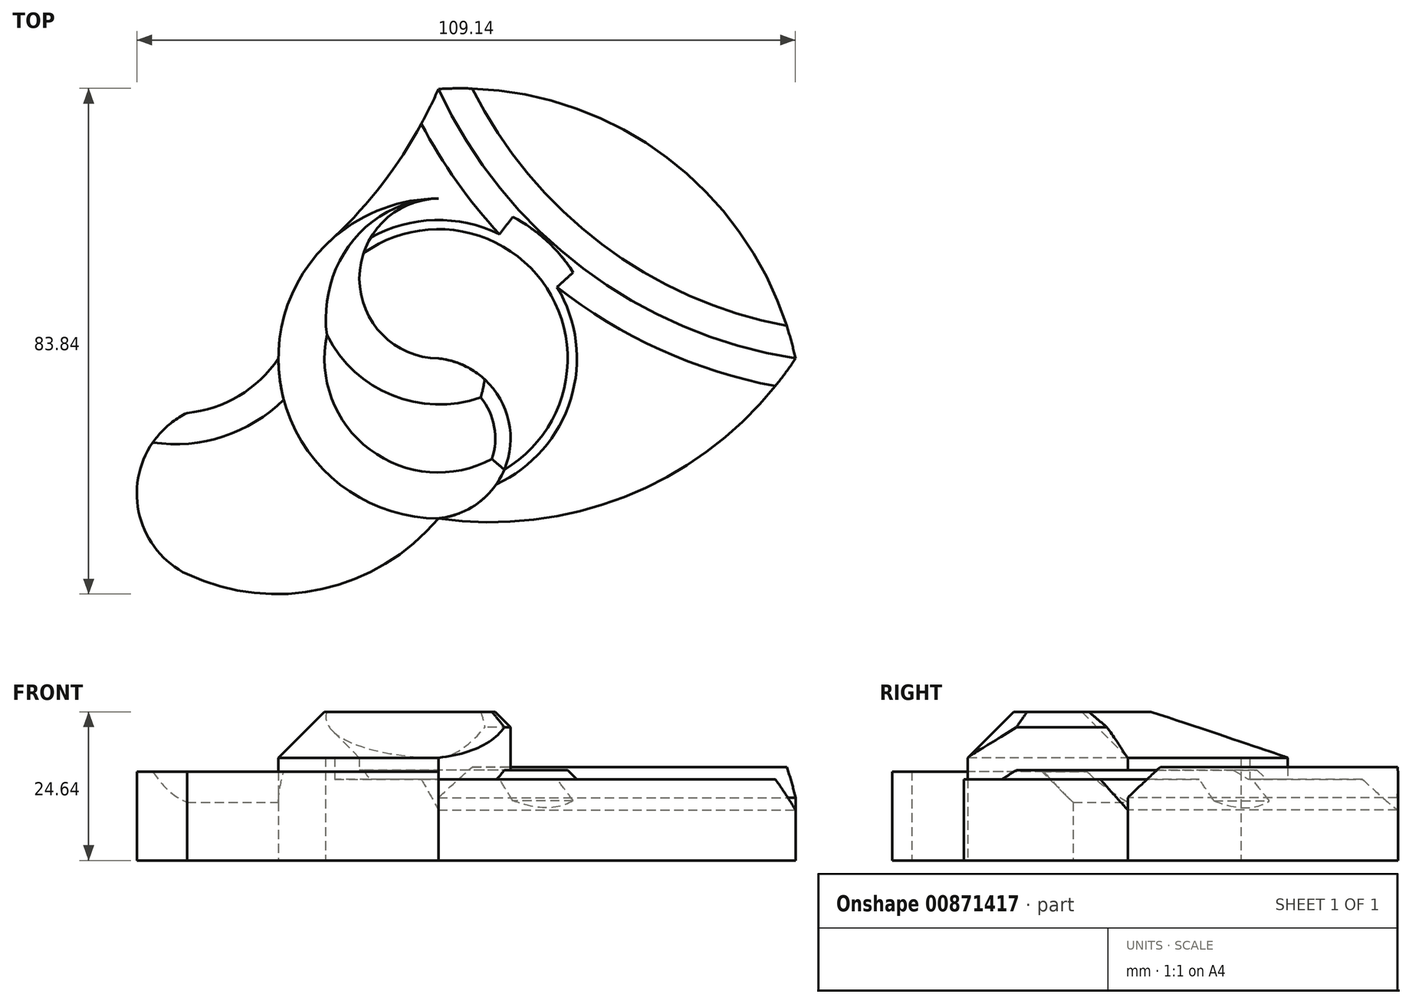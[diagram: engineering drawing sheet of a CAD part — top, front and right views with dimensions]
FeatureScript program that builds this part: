
annotation { "Feature Type Name" : "Feature", "Feature Type Description" : "" }
export const myFeature = defineFeature(function(context is Context, id is Id, definition is map)
    precondition{}
    {
        {
            var Q0;
            Q0=qCreatedBy(makeId("Top.planeOp"),FACE);
            var sketch = newSketch(context, id + "F0", { "sketchPlane" : qUnion([Q0])});
            skCircle(sketch, "E0", {"center": v(0, 0) * mm, "radius": 26.5 * mm});
            skArc(sketch, "E1", {"start": v(0, -26.5) * mm, "mid": v(11.97, -13.25) * mm, "end": v(0, 0) * mm});
            skArc(sketch, "E2", {"start": v(0, 26.5) * mm, "mid": v(-13.1, 13.25) * mm, "end": v(0, 0) * mm});
            skArc(sketch, "E3", {"start": v(-60.7, 0) * mm, "mid": v(-43.6, -9.12) * mm, "end": v(-26.5, 0) * mm});
            skArc(sketch, "E4", {"start": v(0, 44.66) * mm, "mid": v(-40.04, 35.5) * mm, "end": v(-60.7, 0) * mm});
            skArc(sketch, "E5", {"start": v(-60.7, 0) * mm, "mid": v(-24.36, 14.18) * mm, "end": v(0, 44.66) * mm});
            skArc(sketch, "E6", {"start": v(0, -26.5) * mm, "mid": v(33.44, -21.85) * mm, "end": v(59.17, 0) * mm});
            skArc(sketch, "E7", {"start": v(59.17, 0) * mm, "mid": v(37.87, 33.3) * mm, "end": v(0, 44.66) * mm});
            skArc(sketch, "E8", {"start": v(0, 44.66) * mm, "mid": v(24, 14.92) * mm, "end": v(59.17, 0) * mm});
            skArc(sketch, "E9", {"start": v(-41.65, -35.76) * mm, "mid": v(-19.25, -38.22) * mm, "end": v(0, -26.5) * mm});
            skArc(sketch, "E10", {"start": v(-41.65, -9.03) * mm, "mid": v(-49.97, -22.4) * mm, "end": v(-41.65, -35.76) * mm});
            skArc(sketch, "E11", {"start": v(-30.95, -26.5) * mm, "mid": v(-29.13, -13.38) * mm, "end": v(-41.65, -9.03) * mm});
            skArc(sketch, "E12", {"start": v(-38.04, -18.83) * mm, "mid": v(-38.65, -26.5) * mm, "end": v(-30.95, -26.5) * mm});
            skSolve(sketch);
        }
        {
            var Q0;
            {var subQ0=sQuery(id+"F0.wireOp",EDGE,"E1");Q0=makeQuery(id+"F0.imprint","IMPRINT",FACE,{"disambiguationData":[TD([[makeQuery(id+"F0.imprint","IMPRINT",EDGE,{"derivedFrom":subQ0}),1.0]])]});}
            extrude(context, id + "F1", {"entities" : qUnion([Q0]), "depth" : 24.64 * mm, "offsetDistance" : 25.4 * mm});
        }
        {
            var Q0;
            Q0=makeQuery(id+"F1.opExtrude","CAP_EDGE",EDGE,{"disambiguationData":[OSD([sQuery(id+"F0.wireOp",EDGE,"E2")])],"isStart":false});
            var Q1;
            {var subQ0=sQuery(id+"F0.wireOp",EDGE,"E0");var subQ1=makeQuery(id+"F0.imprint","INTERSECT",VERTEX,{"derivedFrom":[subQ0,sQuery(id+"F0.wireOp",EDGE,"E3")]});Q1=makeQuery(id+"F1.opExtrude","CAP_EDGE",EDGE,{"disambiguationData":[OSD([subQ0]),TDD([makeQuery(id+"F0.imprint","IMPRINT",EDGE,{"disambiguationData":[TD([[subQ1,1.0]])],"derivedFrom":subQ0}),makeQuery(id+"F0.imprint","IMPRINT",EDGE,{"disambiguationData":[TD([[subQ1,-1.0]])],"derivedFrom":subQ0})])],"isStart":false});}
            chamfer(context, id + "F2", {"entities" : qUnion([Q0, Q1]), "width" : 7.62 * mm, "tangentPropagation" : true});
        }
        {
            var Q0;
            {var subQ0=sQuery(id+"F0.wireOp",EDGE,"E1");Q0=makeQuery(id+"F0.imprint","IMPRINT",FACE,{"disambiguationData":[TD([[makeQuery(id+"F0.imprint","IMPRINT",EDGE,{"derivedFrom":subQ0}),-1.0]])]});}
            extrude(context, id + "F3", {"entities" : qUnion([Q0]), "operationType" : NewBodyOperationType.ADD, "depth" : 15 * mm, "offsetDistance" : 25.4 * mm});
        }
        {
            var Q0;
            Q0=makeQuery(id+"F1.opExtrude","CAP_EDGE",EDGE,{"disambiguationData":[OSD([sQuery(id+"F0.wireOp",EDGE,"E1")])],"isStart":false});
            chamfer(context, id + "F4", {"entities" : qUnion([Q0]), "width" : 2.54 * mm, "tangentPropagation" : true});
        }
        {
            var Q0;
            {var subQ4=sQuery(id+"F0.wireOp",EDGE,"E6");Q0=makeQuery(id+"F0.imprint","IMPRINT",FACE,{"disambiguationData":[TD([[makeQuery(id+"F0.imprint","IMPRINT",EDGE,{"derivedFrom":subQ4}),1.0]])]});}
            extrude(context, id + "F5", {"entities" : qUnion([Q0]), "operationType" : NewBodyOperationType.ADD, "depth" : 13.46 * mm, "offsetDistance" : 25.4 * mm});
        }
        {
            var Q0;
            Q0=makeQuery(id+"F5.opExtrude","CAP_EDGE",EDGE,{"disambiguationData":[OSD([sQuery(id+"F0.wireOp",EDGE,"E8")])],"isStart":false});
            chamfer(context, id + "F6", {"entities" : qUnion([Q0]), "width" : 5.08 * mm, "tangentPropagation" : true});
        }
        {
            var Q0;
            {var subQ0=sQuery(id+"F0.wireOp",EDGE,"E9");Q0=makeQuery(id+"F0.imprint","IMPRINT",FACE,{"disambiguationData":[TD([[makeQuery(id+"F0.imprint","IMPRINT",EDGE,{"derivedFrom":subQ0}),1.0]])]});}
            extrude(context, id + "F7", {"entities" : qUnion([Q0]), "operationType" : NewBodyOperationType.ADD, "depth" : 14.73 * mm, "offsetDistance" : 25.4 * mm});
        }
        {
            var Q0;
            Q0=makeQuery(id+"F0.imprint","IMPRINT",FACE,{"disambiguationData":[TD([[makeQuery(id+"F0.imprint","IMPRINT",EDGE,{"derivedFrom":sQuery(id+"F0.wireOp",EDGE,"E7")}),1.0]])]});
            extrude(context, id + "F8", {"entities" : qUnion([Q0]), "operationType" : NewBodyOperationType.ADD, "depth" : 15.5 * mm, "offsetDistance" : 25.4 * mm});
        }
        {
            var Q0;
            Q0=makeQuery(id+"F3.opExtrude","CAP_EDGE",EDGE,{"disambiguationData":[OSD([sQuery(id+"F0.wireOp",EDGE,"E0")])],"isStart":false});
            var Q1;
            Q1=makeQuery(id+"F8.opExtrude","CAP_EDGE",EDGE,{"disambiguationData":[OSD([sQuery(id+"F0.wireOp",EDGE,"E8")])],"isStart":false});
            var Q2;
            Q2=makeQuery(id+"F7.opExtrude","CAP_EDGE",EDGE,{"disambiguationData":[OSD([sQuery(id+"F0.wireOp",EDGE,"E3")])],"isStart":false});
            chamfer(context, id + "F9", {"entities" : qUnion([Q0, Q1, Q2]), "width" : 5.08 * mm, "tangentPropagation" : true});
        }
    });
